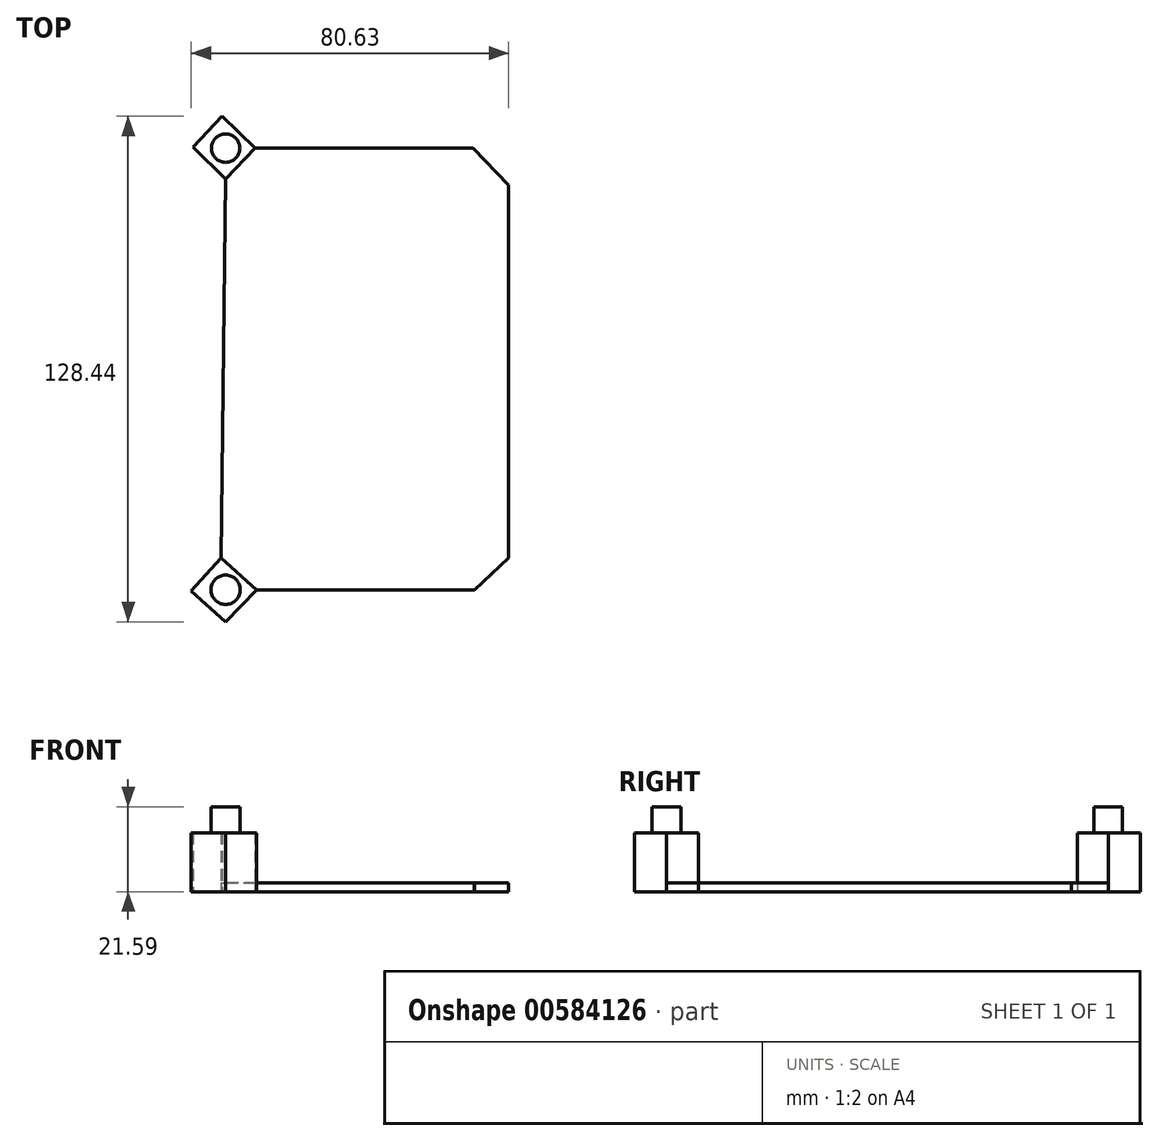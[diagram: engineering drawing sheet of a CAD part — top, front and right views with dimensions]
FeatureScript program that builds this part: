
annotation { "Feature Type Name" : "Feature", "Feature Type Description" : "" }
export const myFeature = defineFeature(function(context is Context, id is Id, definition is map)
    precondition{}
    {
        {
            var Q0;
            Q0=qCreatedBy(makeId("Top.planeOp"),FACE);
            var sketch = newSketch(context, id + "F0", { "sketchPlane" : qUnion([Q0])});
            skLineSegment(sketch, "E0.bottom", {"start": v(27.52, 56.1) * mm, "end": v(-27.82, 56.1) * mm});
            skLineSegment(sketch, "E0.top", {"start": v(27.82, -56.1) * mm, "end": v(-27.52, -56.1) * mm});
            skPoint(sketch, "E0.middle", {"position": v(0, 0) * mm});
            skLineSegment(sketch, "E1", {"start": v(-36.55, -47.98) * mm, "end": v(-35.34, 48.3) * mm});
            skLineSegment(sketch, "E2", {"start": v(36.55, -47.98) * mm, "end": v(36.55, 46.77) * mm});
            skLineSegment(sketch, "E3", {"start": v(-35.34, 48.3) * mm, "end": v(-27.82, 56.1) * mm});
            skLineSegment(sketch, "E4", {"start": v(27.52, 56.1) * mm, "end": v(36.55, 46.77) * mm});
            skLineSegment(sketch, "E5", {"start": v(36.55, -47.98) * mm, "end": v(27.82, -56.1) * mm});
            skLineSegment(sketch, "E6", {"start": v(-27.52, -56.1) * mm, "end": v(-36.55, -47.98) * mm});
            skLineSegment(sketch, "E7", {"start": v(-35.34, 48.3) * mm, "end": v(-43.65, 56.31) * mm});
            skLineSegment(sketch, "E8", {"start": v(-36.55, -47.98) * mm, "end": v(-44.08, -56.36) * mm});
            skLineSegment(sketch, "E9", {"start": v(-44.08, -56.36) * mm, "end": v(-35.34, -64.22) * mm});
            skLineSegment(sketch, "E10", {"start": v(-35.34, -64.22) * mm, "end": v(-27.52, -56.1) * mm});
            skLineSegment(sketch, "E11", {"start": v(-27.82, 56.1) * mm, "end": v(-36.25, 64.22) * mm});
            skLineSegment(sketch, "E12", {"start": v(-36.25, 64.22) * mm, "end": v(-43.65, 56.31) * mm});
            skCircle(sketch, "E13", {"center": v(-35.34, 56.1) * mm, "radius": 3.6 * mm});
            skCircle(sketch, "E14", {"center": v(-35.34, -56.1) * mm, "radius": 3.72 * mm});
            skSolve(sketch);
        }
        {
            var Q0;
            Q0=makeQuery(id+"F0.imprint","IMPRINT",FACE,{"disambiguationData":[TD([[makeQuery(id+"F0.imprint","IMPRINT",EDGE,{"derivedFrom":sQuery(id+"F0.wireOp",EDGE,"E0.bottom")}),1.0]])]});
            extrude(context, id + "F1", {"entities" : qUnion([Q0]), "depth" : 2.3 * mm, "offsetDistance" : 25.4 * mm});
        }
        {
            var Q0;
            Q0=makeQuery(id+"F0.imprint","IMPRINT",FACE,{"disambiguationData":[TD([[makeQuery(id+"F0.imprint","IMPRINT",EDGE,{"derivedFrom":sQuery(id+"F0.wireOp",EDGE,"E3")}),1.0]])]});
            var Q1;
            Q1=makeQuery(id+"F0.imprint","IMPRINT",FACE,{"disambiguationData":[TD([[makeQuery(id+"F0.imprint","IMPRINT",EDGE,{"derivedFrom":sQuery(id+"F0.wireOp",EDGE,"E6")}),1.0]])]});
            extrude(context, id + "F2", {"entities" : qUnion([Q0, Q1]), "operationType" : NewBodyOperationType.ADD, "depth" : 15 * mm, "offsetDistance" : 25.4 * mm});
        }
        {
            var Q0;
            Q0=makeQuery(id+"F0.imprint","IMPRINT",FACE,{"disambiguationData":[TD([[makeQuery(id+"F0.imprint","IMPRINT",EDGE,{"derivedFrom":sQuery(id+"F0.wireOp",EDGE,"E13")}),1.0]])]});
            var Q1;
            Q1=makeQuery(id+"F0.imprint","IMPRINT",FACE,{"disambiguationData":[TD([[makeQuery(id+"F0.imprint","IMPRINT",EDGE,{"derivedFrom":sQuery(id+"F0.wireOp",EDGE,"E14")}),1.0]])]});
            extrude(context, id + "F3", {"entities" : qUnion([Q0, Q1]), "operationType" : NewBodyOperationType.ADD, "depth" : 21.59 * mm, "offsetDistance" : 25.4 * mm});
        }
    });
